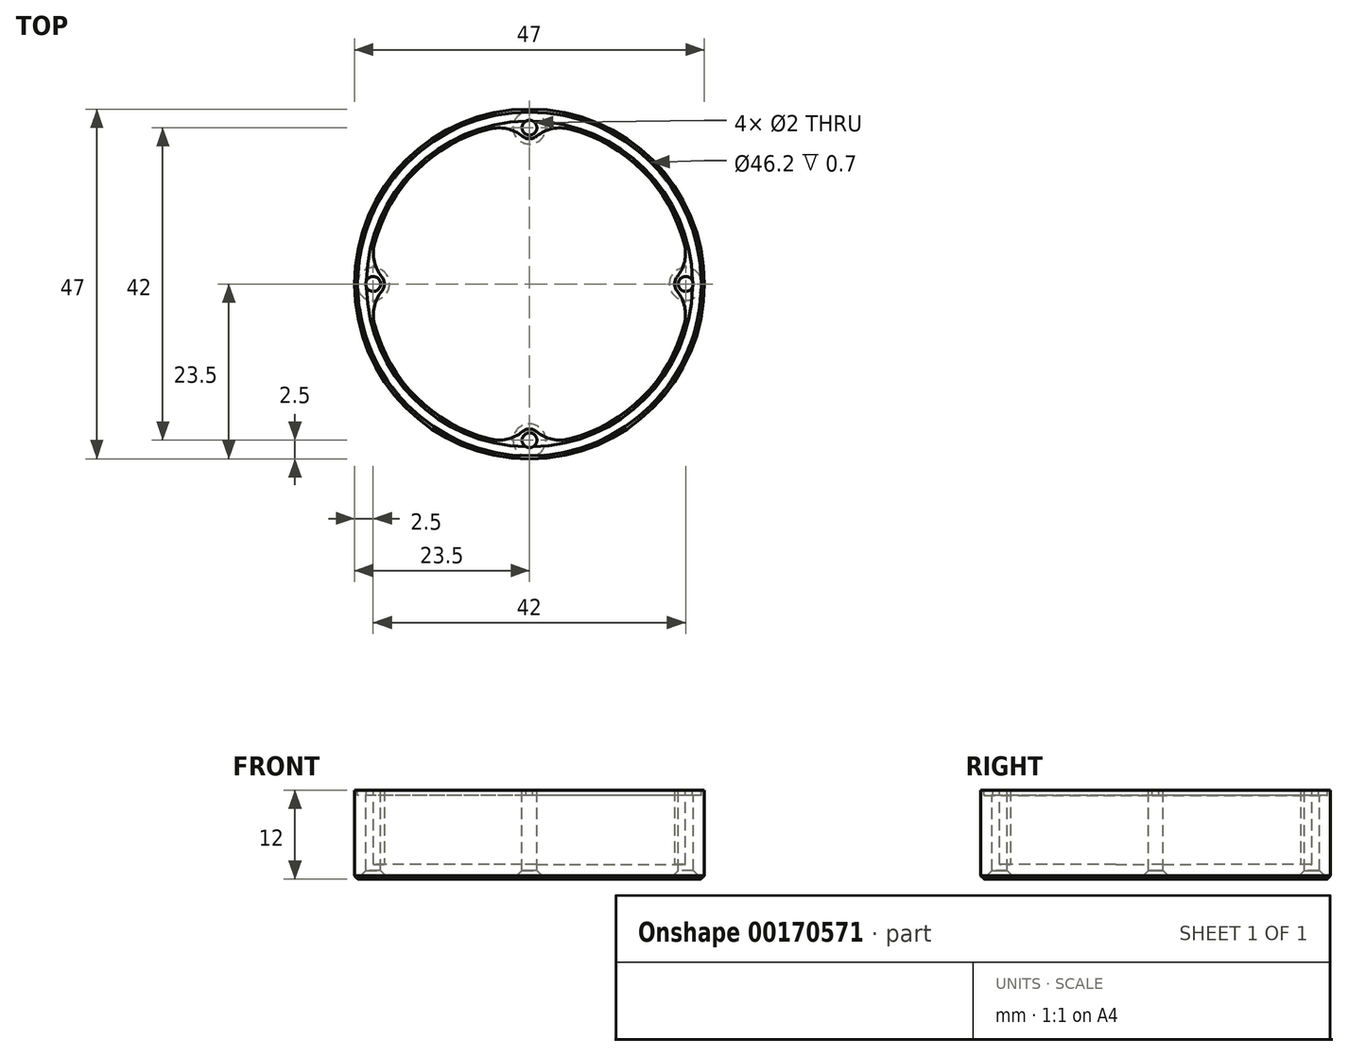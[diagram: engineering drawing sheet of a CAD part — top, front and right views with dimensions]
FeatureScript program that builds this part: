
annotation { "Feature Type Name" : "Feature", "Feature Type Description" : "" }
export const myFeature = defineFeature(function(context is Context, id is Id, definition is map)
    precondition{}
    {
        {
            var Q0;
            Q0=qCreatedBy(makeId("Top.planeOp"),FACE);
            var sketch = newSketch(context, id + "F0", { "sketchPlane" : qUnion([Q0])});
            skCircle(sketch, "E0", {"center": v(0, 0) * mm, "radius": 23.5 * mm});
            skSolve(sketch);
        }
        {
            var Q0;
            Q0 = qSketchRegion(id + "F0", true);
            extrude(context, id + "F1", {"entities" : qUnion([Q0]), "depth" : 12 * mm});
        }
        {
            var Q0;
            Q0=makeQuery(id+"F1.opExtrude","CAP_FACE",FACE,{"disambiguationData":[OSD([sQuery(id+"F0.wireOp",EDGE,"E0")])],"isStart":false});
            shell(context, id + "F2", {"entities" : qUnion([Q0]), "thickness" : 2 * mm});
        }
        {
            var Q0;
            Q0=makeQuery(id+"F1.opExtrude","CAP_EDGE",EDGE,{"disambiguationData":[OSD([sQuery(id+"F0.wireOp",EDGE,"E0")])],"isStart":true});
            chamfer(context, id + "F3", {"entities" : qUnion([Q0]), "width" : 0.5 * mm, "tangentPropagation" : true});
        }
        {
            var Q0;
            {var subQ0=sQuery(id+"F0.wireOp",EDGE,"E0");Q0=makeQuery(id+"F2.opShell","OFFSET_FACE",FACE,{"disambiguationData":[OSD([subQ0]),TDD([makeQuery(id+"F1.opExtrude","CAP_FACE",FACE,{"disambiguationData":[OSD([subQ0])],"isStart":true})])]});}
            var sketch = newSketch(context, id + "F4", { "sketchPlane" : qUnion([Q0])});
            skCircle(sketch, "E1", {"center": v(0, -21) * mm, "radius": 1.5 * mm});
            skCircle(sketch, "E2.1.0", {"center": v(21, 0) * mm, "radius": 1.5 * mm});
            skCircle(sketch, "E2.2.0", {"center": v(0, 21) * mm, "radius": 1.5 * mm});
            skCircle(sketch, "E2.3.0", {"center": v(-21, 0) * mm, "radius": 1.5 * mm});
            skPoint(sketch, "E2.center", {"position": v(0, 0) * mm});
            skSolve(sketch);
        }
        {
            var Q0;
            Q0 = qSketchRegion(id + "F4", true);
            var Q1;
            {var subQ0=sQuery(id+"F0.wireOp",EDGE,"E0");Q1=makeQuery(id+"F10.boolean.opBoolean","SPLIT",FACE,{"disambiguationData":[TD([makeQuery(id+"F10.opExtrude","SWEPT_FACE",FACE,{"disambiguationData":[OSD([sQuery(id+"F9.wireOp",EDGE,"E5")])]})])],"derivedFrom":makeQuery(id+"F1.opExtrude","CAP_FACE",FACE,{"disambiguationData":[OSD([subQ0])],"isStart":false})});}
            extrude(context, id + "F5", {"entities" : qUnion([Q0]), "operationType" : NewBodyOperationType.ADD, "endBound" : BoundingType.UP_TO_SURFACE, "endBoundEntityFace" : qUnion([Q1]), "depth" : 25 * mm});
        }
        {
            var Q0;
            {var subQ0=sQuery(id+"F0.wireOp",EDGE,"E0");Q0=makeQuery(id+"F5.boolean.opBoolean","INTERSECT",EDGE,{"disambiguationData":[OD(1.0)],"derivedFrom":[makeQuery(id+"F2.opShell","OFFSET_FACE",FACE,{"disambiguationData":[OSD([subQ0]),TDD([makeQuery(id+"F1.opExtrude","SWEPT_FACE",FACE,{"disambiguationData":[OSD([subQ0])]})])]}),makeQuery(id+"F5.opExtrude","SWEPT_FACE",FACE,{"disambiguationData":[OSD([sQuery(id+"F4.wireOp",EDGE,"E2.3.0")])]})]});}
            var Q1;
            {var subQ0=sQuery(id+"F0.wireOp",EDGE,"E0");Q1=makeQuery(id+"F5.boolean.opBoolean","INTERSECT",EDGE,{"disambiguationData":[OD(0.0)],"derivedFrom":[makeQuery(id+"F2.opShell","OFFSET_FACE",FACE,{"disambiguationData":[OSD([subQ0]),TDD([makeQuery(id+"F1.opExtrude","SWEPT_FACE",FACE,{"disambiguationData":[OSD([subQ0])]})])]}),makeQuery(id+"F5.opExtrude","SWEPT_FACE",FACE,{"disambiguationData":[OSD([sQuery(id+"F4.wireOp",EDGE,"E2.3.0")])]})]});}
            var Q2;
            {var subQ0=sQuery(id+"F0.wireOp",EDGE,"E0");Q2=makeQuery(id+"F5.boolean.opBoolean","INTERSECT",EDGE,{"disambiguationData":[OD(0.0)],"derivedFrom":[makeQuery(id+"F2.opShell","OFFSET_FACE",FACE,{"disambiguationData":[OSD([subQ0]),TDD([makeQuery(id+"F1.opExtrude","SWEPT_FACE",FACE,{"disambiguationData":[OSD([subQ0])]})])]}),makeQuery(id+"F5.opExtrude","SWEPT_FACE",FACE,{"disambiguationData":[OSD([sQuery(id+"F4.wireOp",EDGE,"E2.2.0")])]})]});}
            var Q3;
            {var subQ0=sQuery(id+"F0.wireOp",EDGE,"E0");Q3=makeQuery(id+"F5.boolean.opBoolean","INTERSECT",EDGE,{"disambiguationData":[OD(1.0)],"derivedFrom":[makeQuery(id+"F2.opShell","OFFSET_FACE",FACE,{"disambiguationData":[OSD([subQ0]),TDD([makeQuery(id+"F1.opExtrude","SWEPT_FACE",FACE,{"disambiguationData":[OSD([subQ0])]})])]}),makeQuery(id+"F5.opExtrude","SWEPT_FACE",FACE,{"disambiguationData":[OSD([sQuery(id+"F4.wireOp",EDGE,"E2.2.0")])]})]});}
            var Q4;
            {var subQ0=sQuery(id+"F0.wireOp",EDGE,"E0");Q4=makeQuery(id+"F5.boolean.opBoolean","INTERSECT",EDGE,{"disambiguationData":[OD(0.0)],"derivedFrom":[makeQuery(id+"F2.opShell","OFFSET_FACE",FACE,{"disambiguationData":[OSD([subQ0]),TDD([makeQuery(id+"F1.opExtrude","SWEPT_FACE",FACE,{"disambiguationData":[OSD([subQ0])]})])]}),makeQuery(id+"F5.opExtrude","SWEPT_FACE",FACE,{"disambiguationData":[OSD([sQuery(id+"F4.wireOp",EDGE,"E2.1.0")])]})]});}
            var Q5;
            {var subQ0=sQuery(id+"F0.wireOp",EDGE,"E0");Q5=makeQuery(id+"F5.boolean.opBoolean","INTERSECT",EDGE,{"disambiguationData":[OD(1.0)],"derivedFrom":[makeQuery(id+"F2.opShell","OFFSET_FACE",FACE,{"disambiguationData":[OSD([subQ0]),TDD([makeQuery(id+"F1.opExtrude","SWEPT_FACE",FACE,{"disambiguationData":[OSD([subQ0])]})])]}),makeQuery(id+"F5.opExtrude","SWEPT_FACE",FACE,{"disambiguationData":[OSD([sQuery(id+"F4.wireOp",EDGE,"E2.1.0")])]})]});}
            var Q6;
            {var subQ0=sQuery(id+"F0.wireOp",EDGE,"E0");Q6=makeQuery(id+"F5.boolean.opBoolean","INTERSECT",EDGE,{"disambiguationData":[OD(1.0)],"derivedFrom":[makeQuery(id+"F2.opShell","OFFSET_FACE",FACE,{"disambiguationData":[OSD([subQ0]),TDD([makeQuery(id+"F1.opExtrude","SWEPT_FACE",FACE,{"disambiguationData":[OSD([subQ0])]})])]}),makeQuery(id+"F5.opExtrude","SWEPT_FACE",FACE,{"disambiguationData":[OSD([sQuery(id+"F4.wireOp",EDGE,"E1")])]})]});}
            var Q7;
            {var subQ0=sQuery(id+"F0.wireOp",EDGE,"E0");Q7=makeQuery(id+"F5.boolean.opBoolean","INTERSECT",EDGE,{"disambiguationData":[OD(0.0)],"derivedFrom":[makeQuery(id+"F2.opShell","OFFSET_FACE",FACE,{"disambiguationData":[OSD([subQ0]),TDD([makeQuery(id+"F1.opExtrude","SWEPT_FACE",FACE,{"disambiguationData":[OSD([subQ0])]})])]}),makeQuery(id+"F5.opExtrude","SWEPT_FACE",FACE,{"disambiguationData":[OSD([sQuery(id+"F4.wireOp",EDGE,"E1")])]})]});}
            fillet(context, id + "F6", {"entities" : qUnion([Q0, Q1, Q2, Q3, Q4, Q5, Q6, Q7]), "radius" : 5 * mm, "tangentPropagation" : true, "allowEdgeOverflow" : false});
        }
        {
            var Q0;
            {var subQ0=sQuery(id+"F4.wireOp",EDGE,"E2.2.0");var subQ2=sQuery(id+"F0.wireOp",EDGE,"E0");var subQ4=sQuery(id+"F4.wireOp",EDGE,"E2.1.0");var subQ6=sQuery(id+"F4.wireOp",EDGE,"E2.3.0");var subQ8=sQuery(id+"F4.wireOp",EDGE,"E1");var subQ9=makeQuery(id+"F5.opExtrude","SWEPT_FACE",FACE,{"disambiguationData":[OSD([subQ8])]});Q0=makeQuery(id+"F10.boolean.opBoolean","SPLIT",FACE,{"disambiguationData":[TD([subQ9])],"derivedFrom":makeQuery(id+"F5.boolean.opBoolean","MERGE",FACE,{"derivedFrom":[makeQuery(id+"F1.opExtrude","CAP_FACE",FACE,{"disambiguationData":[OSD([subQ2])],"isStart":false}),makeQuery(id+"F5.opExtrude","CAP_FACE",FACE,{"disambiguationData":[OSD([subQ2]),ownerDisambiguation([makeQuery(id+"F5.opExtrude","SWEPT_BODY",BODY,{"disambiguationData":[OSD([subQ8])]})])],"isStart":false}),makeQuery(id+"F5.opExtrude","CAP_FACE",FACE,{"disambiguationData":[OSD([subQ2]),ownerDisambiguation([makeQuery(id+"F5.opExtrude","SWEPT_BODY",BODY,{"disambiguationData":[OSD([subQ4])]})])],"isStart":false}),makeQuery(id+"F5.opExtrude","CAP_FACE",FACE,{"disambiguationData":[OSD([subQ2]),ownerDisambiguation([makeQuery(id+"F5.opExtrude","SWEPT_BODY",BODY,{"disambiguationData":[OSD([subQ0])]})])],"isStart":false}),makeQuery(id+"F5.opExtrude","CAP_FACE",FACE,{"disambiguationData":[OSD([subQ2]),ownerDisambiguation([makeQuery(id+"F5.opExtrude","SWEPT_BODY",BODY,{"disambiguationData":[OSD([subQ6])]})])],"isStart":false})]})});}
            var sketch = newSketch(context, id + "F7", { "sketchPlane" : qUnion([Q0])});
            skCircle(sketch, "E3", {"center": v(0, -21) * mm, "radius": 1 * mm});
            skCircle(sketch, "E4.1.0", {"center": v(21, 0) * mm, "radius": 1 * mm});
            skCircle(sketch, "E4.2.0", {"center": v(0, 21) * mm, "radius": 1 * mm});
            skCircle(sketch, "E4.3.0", {"center": v(-21, 0) * mm, "radius": 1 * mm});
            skPoint(sketch, "E4.center", {"position": v(0, 0) * mm});
            skSolve(sketch);
        }
        {
            var Q0;
            Q0 = qSketchRegion(id + "F7", true);
            extrude(context, id + "F8", {"entities" : qUnion([Q0]), "operationType" : NewBodyOperationType.REMOVE, "endBound" : BoundingType.THROUGH_ALL, "oppositeDirection" : true, "depth" : 10 * mm});
        }
        {
            var Q0;
            Q0=makeQuery(id+"F1.opExtrude","CAP_FACE",FACE,{"disambiguationData":[OSD([sQuery(id+"F0.wireOp",EDGE,"E0")])],"isStart":false});
            var sketch = newSketch(context, id + "F9", { "sketchPlane" : qUnion([Q0])});
            skCircle(sketch, "E5", {"center": v(0, 0) * mm, "radius": 21.9 * mm});
            skCircle(sketch, "E6", {"center": v(0, 0) * mm, "radius": 23.1 * mm});
            skSolve(sketch);
        }
        {
            var Q0;
            Q0 = qSketchRegion(id + "F9", true);
            extrude(context, id + "F10", {"entities" : qUnion([Q0]), "operationType" : NewBodyOperationType.REMOVE, "oppositeDirection" : true, "depth" : 0.7 * mm});
        }
        {
            var Q0;
            Q0=makeQuery(id+"F8.boolean.opBoolean","INTERSECT",EDGE,{"derivedFrom":[makeQuery(id+"F1.opExtrude","CAP_FACE",FACE,{"disambiguationData":[OSD([sQuery(id+"F0.wireOp",EDGE,"E0")])],"isStart":true}),makeQuery(id+"F8.opExtrude","SWEPT_FACE",FACE,{"disambiguationData":[OSD([sQuery(id+"F7.wireOp",EDGE,"E4.2.0")])]})]});
            var Q1;
            Q1=makeQuery(id+"F8.boolean.opBoolean","INTERSECT",EDGE,{"derivedFrom":[makeQuery(id+"F1.opExtrude","CAP_FACE",FACE,{"disambiguationData":[OSD([sQuery(id+"F0.wireOp",EDGE,"E0")])],"isStart":true}),makeQuery(id+"F8.opExtrude","SWEPT_FACE",FACE,{"disambiguationData":[OSD([sQuery(id+"F7.wireOp",EDGE,"E4.1.0")])]})]});
            var Q2;
            Q2=makeQuery(id+"F8.boolean.opBoolean","INTERSECT",EDGE,{"derivedFrom":[makeQuery(id+"F1.opExtrude","CAP_FACE",FACE,{"disambiguationData":[OSD([sQuery(id+"F0.wireOp",EDGE,"E0")])],"isStart":true}),makeQuery(id+"F8.opExtrude","SWEPT_FACE",FACE,{"disambiguationData":[OSD([sQuery(id+"F7.wireOp",EDGE,"E3")])]})]});
            var Q3;
            Q3=makeQuery(id+"F8.boolean.opBoolean","INTERSECT",EDGE,{"derivedFrom":[makeQuery(id+"F1.opExtrude","CAP_FACE",FACE,{"disambiguationData":[OSD([sQuery(id+"F0.wireOp",EDGE,"E0")])],"isStart":true}),makeQuery(id+"F8.opExtrude","SWEPT_FACE",FACE,{"disambiguationData":[OSD([sQuery(id+"F7.wireOp",EDGE,"E4.3.0")])]})]});
            chamfer(context, id + "F11", {"entities" : qUnion([Q0, Q1, Q2, Q3]), "chamferType" : ChamferType.OFFSET_ANGLE, "width" : 1.2 * mm, "oppositeDirection" : false, "angle" : 45 * degree, "tangentPropagation" : true});
        }
    });
